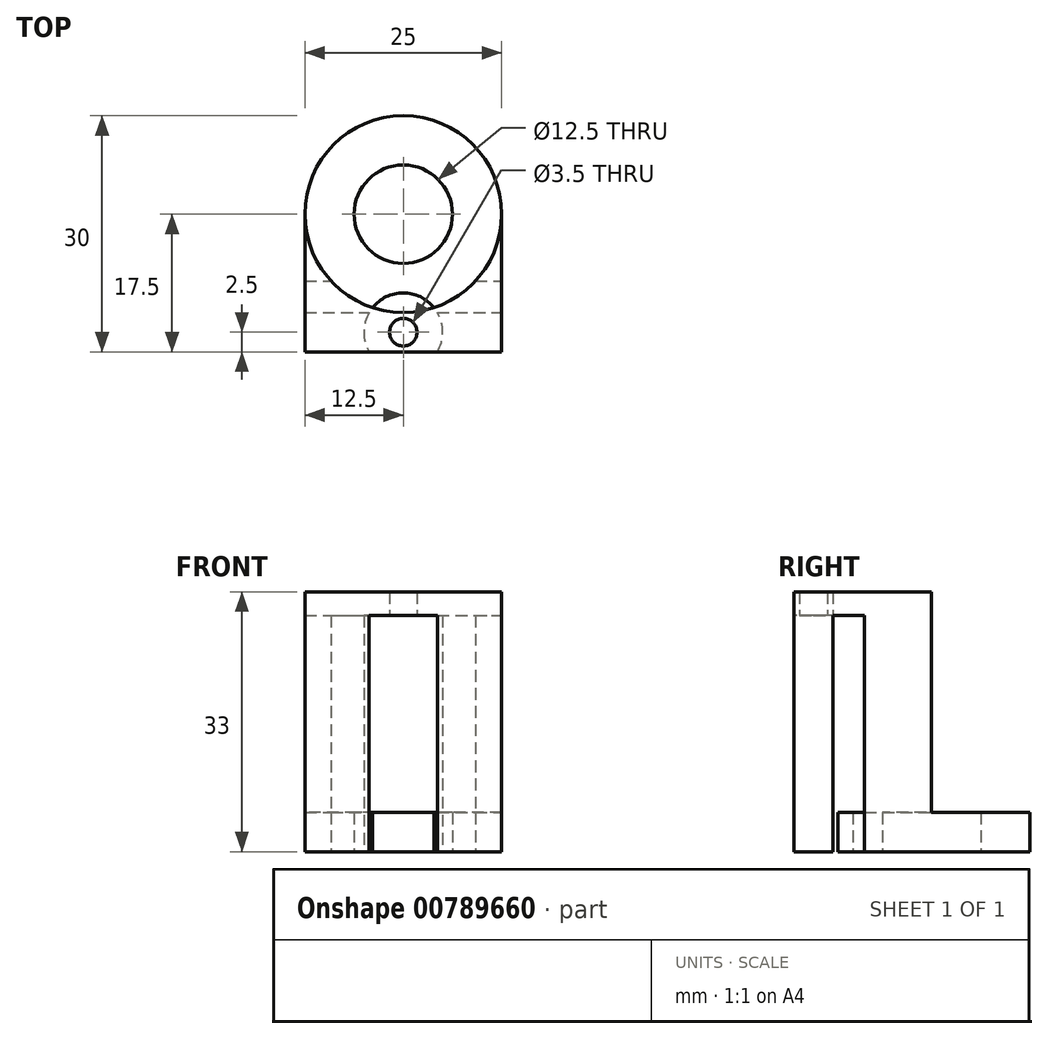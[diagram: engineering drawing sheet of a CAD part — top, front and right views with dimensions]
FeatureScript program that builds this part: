
annotation { "Feature Type Name" : "Feature", "Feature Type Description" : "" }
export const myFeature = defineFeature(function(context is Context, id is Id, definition is map)
    precondition{}
    {
        {
            var Q0;
            Q0=qCreatedBy(makeId("Top.planeOp"),FACE);
            var sketch = newSketch(context, id + "F0", { "sketchPlane" : qUnion([Q0])});
            skCircle(sketch, "E0", {"center": v(0, 0) * mm, "radius": 10 * mm});
            skCircle(sketch, "E1", {"center": v(0, 0) * mm, "radius": 12.5 * mm});
            skCircle(sketch, "E2", {"center": v(0, 0) * mm, "radius": 6.25 * mm});
            skLineSegment(sketch, "E3.bottom", {"start": v(-12.5, 0) * mm, "end": v(12.5, 0) * mm});
            skLineSegment(sketch, "E3.top", {"start": v(-12.5, -12.5) * mm, "end": v(12.5, -12.5) * mm});
            skLineSegment(sketch, "E3.left", {"start": v(-12.5, 0) * mm, "end": v(-12.5, -12.5) * mm});
            skLineSegment(sketch, "E3.right", {"start": v(12.5, 0) * mm, "end": v(12.5, -12.5) * mm});
            skLineSegment(sketch, "E4.top", {"start": v(-12.5, -8.5) * mm, "end": v(12.5, -8.5) * mm});
            skLineSegment(sketch, "E4.left", {"start": v(-12.5, -12.5) * mm, "end": v(-12.5, -8.5) * mm});
            skLineSegment(sketch, "E4.right", {"start": v(12.5, -12.5) * mm, "end": v(12.5, -8.5) * mm});
            skCircle(sketch, "E5", {"center": v(0, -15) * mm, "radius": 5 * mm});
            skLineSegment(sketch, "E6.top", {"start": v(-12.5, -17.5) * mm, "end": v(12.5, -17.5) * mm});
            skLineSegment(sketch, "E6.left", {"start": v(-12.5, -12.5) * mm, "end": v(-12.5, -17.5) * mm});
            skLineSegment(sketch, "E6.right", {"start": v(12.5, -12.5) * mm, "end": v(12.5, -17.5) * mm});
            skPoint(sketch, "E7", {"position": v(0, -12.5) * mm});
            skPoint(sketch, "E8", {"position": v(0, -17.5) * mm});
            skSolve(sketch);
        }
        {
            var Q0;
            Q0=makeQuery(id+"F0.imprint","IMPRINT",FACE,{"disambiguationData":[TD([[makeQuery(id+"F0.imprint","IMPRINT",EDGE,{"derivedFrom":sQuery(id+"F0.wireOp",EDGE,"E0")}),1.0]])]});
            var Q1;
            Q1=makeQuery(id+"F0.imprint","IMPRINT",FACE,{"disambiguationData":[TD([[makeQuery(id+"F0.imprint","IMPRINT",EDGE,{"derivedFrom":sQuery(id+"F0.wireOp",EDGE,"E0")}),-1.0]])]});
            var Q2;
            {var subQ0=sQuery(id+"F0.wireOp",EDGE,"E3.bottom");var subQ3=sQuery(id+"F0.wireOp",EDGE,"E0");var subQ4=makeQuery(id+"F0.imprint","INTERSECT",VERTEX,{"disambiguationData":[OD(0.0)],"derivedFrom":[subQ3,subQ0]});Q2=makeQuery(id+"F0.imprint","IMPRINT",FACE,{"disambiguationData":[TD([[makeQuery(id+"F0.imprint","IMPRINT",EDGE,{"disambiguationData":[TD([[subQ4,-1.0]])],"derivedFrom":subQ3}),-1.0]])]});}
            var Q3;
            {var subQ0=sQuery(id+"F0.wireOp",EDGE,"E5");var subQ1=sQuery(id+"F0.wireOp",EDGE,"E1");var subQ2=makeQuery(id+"F0.imprint","INTERSECT",VERTEX,{"disambiguationData":[OD(1.0)],"derivedFrom":[subQ1,subQ0]});Q3=makeQuery(id+"F0.imprint","IMPRINT",FACE,{"disambiguationData":[TD([[makeQuery(id+"F0.imprint","IMPRINT",EDGE,{"disambiguationData":[TD([[subQ2,-1.0]])],"derivedFrom":subQ1}),1.0]])]});}
            var Q4;
            {var subQ0=sQuery(id+"F0.wireOp",EDGE,"E4.top");var subQ1=sQuery(id+"F0.wireOp",EDGE,"E1");var subQ2=makeQuery(id+"F0.imprint","INTERSECT",VERTEX,{"disambiguationData":[OD(0.0)],"derivedFrom":[subQ1,subQ0]});Q4=makeQuery(id+"F0.imprint","IMPRINT",FACE,{"disambiguationData":[TD([[makeQuery(id+"F0.imprint","IMPRINT",EDGE,{"disambiguationData":[TD([[subQ2,-1.0]])],"derivedFrom":subQ1}),1.0]])]});}
            var Q5;
            {var subQ0=sQuery(id+"F0.wireOp",EDGE,"E3.bottom");var subQ1=sQuery(id+"F0.wireOp",EDGE,"E0");var subQ2=makeQuery(id+"F0.imprint","INTERSECT",VERTEX,{"disambiguationData":[OD(0.0)],"derivedFrom":[subQ1,subQ0]});Q5=makeQuery(id+"F0.imprint","IMPRINT",FACE,{"disambiguationData":[TD([[makeQuery(id+"F0.imprint","IMPRINT",EDGE,{"disambiguationData":[TD([[subQ2,1.0]])],"derivedFrom":subQ1}),1.0]])]});}
            var Q6;
            {var subQ0=sQuery(id+"F0.wireOp",EDGE,"E3.bottom");var subQ1=sQuery(id+"F0.wireOp",EDGE,"E0");var subQ2=makeQuery(id+"F0.imprint","INTERSECT",VERTEX,{"disambiguationData":[OD(0.0)],"derivedFrom":[subQ1,subQ0]});Q6=makeQuery(id+"F0.imprint","IMPRINT",FACE,{"disambiguationData":[TD([[makeQuery(id+"F0.imprint","IMPRINT",EDGE,{"disambiguationData":[TD([[subQ2,-1.0]])],"derivedFrom":subQ1}),1.0]])]});}
            extrude(context, id + "F1", {"entities" : qUnion([Q0, Q1, Q2, Q3, Q4, Q5, Q6]), "depth" : 5 * mm, "offsetDistance" : 25 * mm});
        }
        {
            var Q0;
            {var subQ0=sQuery(id+"F0.wireOp",EDGE,"E3.left");Q0=makeQuery(id+"F0.imprint","IMPRINT",FACE,{"disambiguationData":[TD([[makeQuery(id+"F0.imprint","IMPRINT",EDGE,{"derivedFrom":subQ0}),1.0]])]});}
            var Q1;
            {var subQ0=sQuery(id+"F0.wireOp",EDGE,"E3.right");Q1=makeQuery(id+"F0.imprint","IMPRINT",FACE,{"disambiguationData":[TD([[makeQuery(id+"F0.imprint","IMPRINT",EDGE,{"derivedFrom":subQ0}),-1.0]])]});}
            var Q2;
            {var subQ5=sQuery(id+"F0.wireOp",EDGE,"E4.right");Q2=makeQuery(id+"F0.imprint","IMPRINT",FACE,{"disambiguationData":[TD([[makeQuery(id+"F0.imprint","IMPRINT",EDGE,{"derivedFrom":subQ5}),1.0]])]});}
            var Q3;
            {var subQ5=sQuery(id+"F0.wireOp",EDGE,"E4.left");Q3=makeQuery(id+"F0.imprint","IMPRINT",FACE,{"disambiguationData":[TD([[makeQuery(id+"F0.imprint","IMPRINT",EDGE,{"derivedFrom":subQ5}),-1.0]])]});}
            var Q4;
            {var subQ5=sQuery(id+"F0.wireOp",EDGE,"E6.left");Q4=makeQuery(id+"F0.imprint","IMPRINT",FACE,{"disambiguationData":[TD([[makeQuery(id+"F0.imprint","IMPRINT",EDGE,{"derivedFrom":subQ5}),1.0]])]});}
            var Q5;
            {var subQ5=sQuery(id+"F0.wireOp",EDGE,"E6.right");Q5=makeQuery(id+"F0.imprint","IMPRINT",FACE,{"disambiguationData":[TD([[makeQuery(id+"F0.imprint","IMPRINT",EDGE,{"derivedFrom":subQ5}),-1.0]])]});}
            extrude(context, id + "F2", {"entities" : qUnion([Q0, Q1, Q2, Q3, Q4, Q5]), "operationType" : NewBodyOperationType.ADD, "depth" : 30 * mm, "offsetDistance" : 25 * mm});
        }
        {
            var Q0;
            Q0=makeQuery(id+"F2.opExtrude","CAP_FACE",FACE,{"disambiguationData":[OSD([sQuery(id+"F0.wireOp",EDGE,"E1"),sQuery(id+"F0.wireOp",EDGE,"E3.left"),sQuery(id+"F0.wireOp",EDGE,"E3.right"),sQuery(id+"F0.wireOp",EDGE,"E3.top"),sQuery(id+"F0.wireOp",EDGE,"E4.top"),sQuery(id+"F0.wireOp",EDGE,"E4.left"),sQuery(id+"F0.wireOp",EDGE,"E4.right")])],"isStart":false});
            var sketch = newSketch(context, id + "F3", { "sketchPlane" : qUnion([Q0])});
            skLineSegment(sketch, "E9.0", {"start": v(-12.5, 0) * mm, "end": v(-12.5, -12.5) * mm});
            skLineSegment(sketch, "E10.0", {"start": v(-12.5, -12.5) * mm, "end": v(12.5, -12.5) * mm});
            skLineSegment(sketch, "E11.0", {"start": v(12.5, 0) * mm, "end": v(12.5, -12.5) * mm});
            skPoint(sketch, "E12.0", {"position": v(0, -17.5) * mm});
            skLineSegment(sketch, "E13.0", {"start": v(-12.5, -12.5) * mm, "end": v(-12.5, -17.5) * mm});
            skLineSegment(sketch, "E14.0", {"start": v(-12.5, -17.5) * mm, "end": v(12.5, -17.5) * mm});
            skLineSegment(sketch, "E15.0", {"start": v(12.5, -12.5) * mm, "end": v(12.5, -17.5) * mm});
            skCircle(sketch, "E16", {"center": v(0, -15) * mm, "radius": 1.75 * mm});
            skCircle(sketch, "E17.0", {"center": v(0, 0) * mm, "radius": 12.5 * mm});
            skSolve(sketch);
        }
        {
            var Q0;
            Q0=makeQuery(id+"F3.imprint","IMPRINT",FACE,{"disambiguationData":[TD([[makeQuery(id+"F3.imprint","IMPRINT",EDGE,{"derivedFrom":sQuery(id+"F3.wireOp",EDGE,"E16")}),-1.0]])]});
            var Q1;
            {var subQ0=sQuery(id+"F3.wireOp",EDGE,"E9.0");Q1=makeQuery(id+"F3.imprint","IMPRINT",FACE,{"disambiguationData":[TD([[makeQuery(id+"F3.imprint","IMPRINT",EDGE,{"derivedFrom":subQ0}),1.0]])]});}
            var Q2;
            {var subQ0=sQuery(id+"F3.wireOp",EDGE,"E13.0");Q2=makeQuery(id+"F3.imprint","IMPRINT",FACE,{"disambiguationData":[TD([[makeQuery(id+"F3.imprint","IMPRINT",EDGE,{"derivedFrom":subQ0}),1.0]])]});}
            var Q3;
            {var subQ0=sQuery(id+"F3.wireOp",EDGE,"E11.0");Q3=makeQuery(id+"F3.imprint","IMPRINT",FACE,{"disambiguationData":[TD([[makeQuery(id+"F3.imprint","IMPRINT",EDGE,{"derivedFrom":subQ0}),-1.0]])]});}
            var Q4;
            {var subQ0=sQuery(id+"F3.wireOp",EDGE,"E15.0");Q4=makeQuery(id+"F3.imprint","IMPRINT",FACE,{"disambiguationData":[TD([[makeQuery(id+"F3.imprint","IMPRINT",EDGE,{"derivedFrom":subQ0}),-1.0]])]});}
            var Q5;
            {var subQ0=sQuery(id+"F3.wireOp",EDGE,"E17.0");var subQ1=sQuery(id+"F3.wireOp",EDGE,"E10.0");var subQ2=makeQuery(id+"F3.imprint","INTERSECT",VERTEX,{"derivedFrom":[subQ1,subQ0]});Q5=makeQuery(id+"F3.imprint","IMPRINT",FACE,{"disambiguationData":[TD([[makeQuery(id+"F3.imprint","IMPRINT",EDGE,{"disambiguationData":[TD([[subQ2,1.0]])],"derivedFrom":subQ1}),1.0]])]});}
            var Q6;
            {var subQ0=sQuery(id+"F3.wireOp",EDGE,"E17.0");var subQ1=sQuery(id+"F3.wireOp",EDGE,"E10.0");var subQ2=makeQuery(id+"F3.imprint","INTERSECT",VERTEX,{"derivedFrom":[subQ1,subQ0]});Q6=makeQuery(id+"F3.imprint","IMPRINT",FACE,{"disambiguationData":[TD([[makeQuery(id+"F3.imprint","IMPRINT",EDGE,{"disambiguationData":[TD([[subQ2,-1.0]])],"derivedFrom":subQ1}),1.0]])]});}
            extrude(context, id + "F4", {"entities" : qUnion([Q0, Q1, Q2, Q3, Q4, Q5, Q6]), "operationType" : NewBodyOperationType.ADD, "depth" : 3 * mm, "offsetDistance" : 25 * mm});
        }
    });
